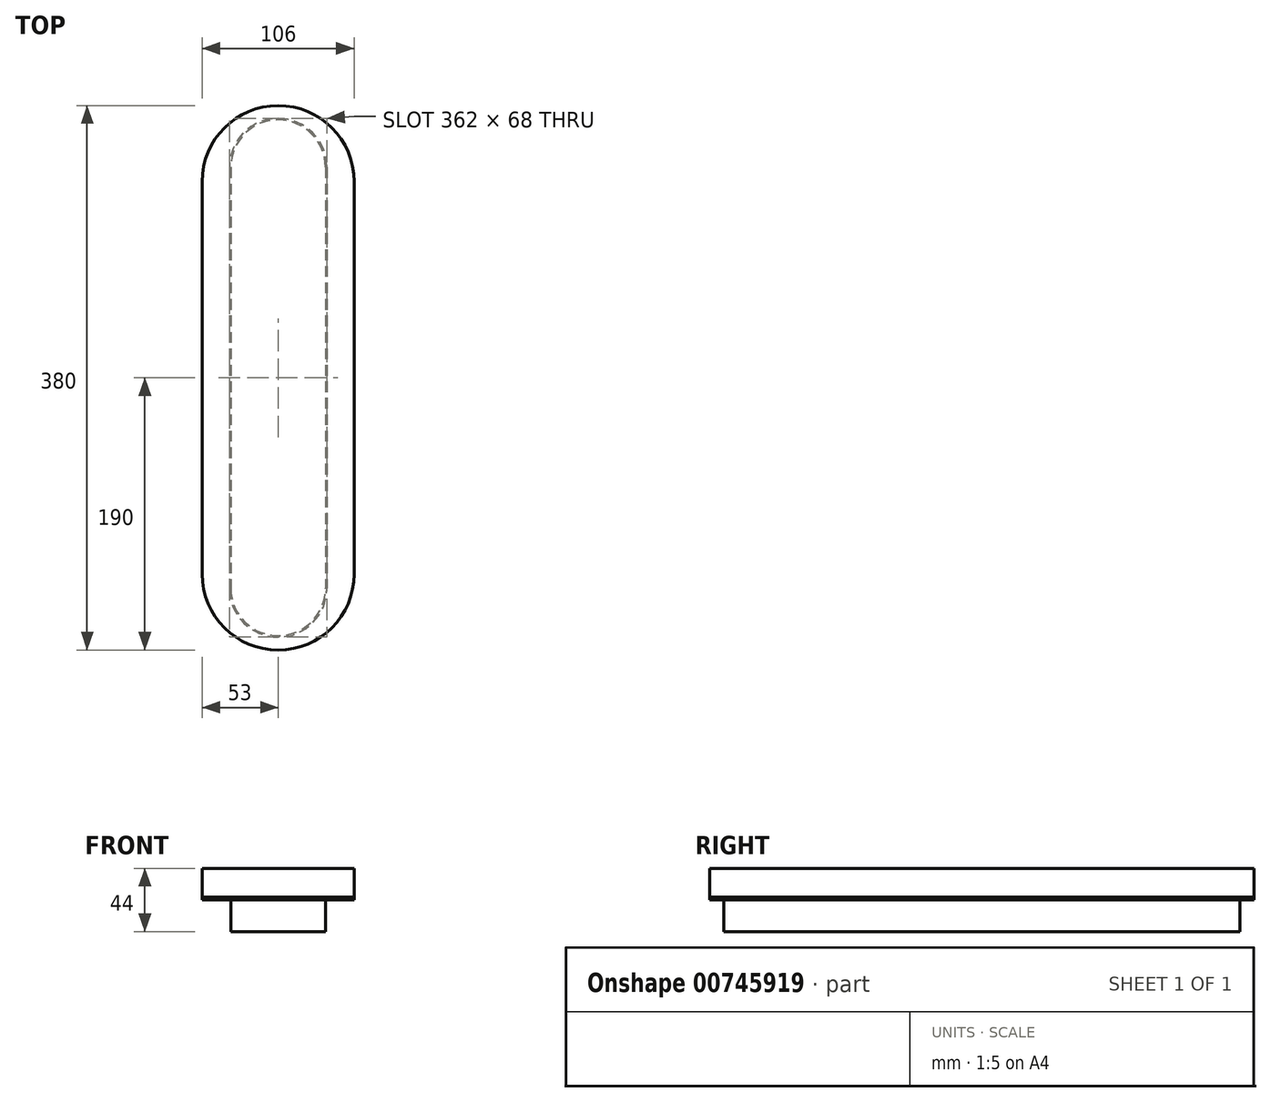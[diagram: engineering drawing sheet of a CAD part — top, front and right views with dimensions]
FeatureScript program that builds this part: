
annotation { "Feature Type Name" : "Feature", "Feature Type Description" : "" }
export const myFeature = defineFeature(function(context is Context, id is Id, definition is map)
    precondition{}
    {
        {
            var Q0;
            Q0=qCreatedBy(makeId("Top.planeOp"),FACE);
            var sketch = newSketch(context, id + "F0", { "sketchPlane" : qUnion([Q0])});
            skLineSegment(sketch, "E0.bottom", {"start": v(33, 147) * mm, "end": v(-33, 147) * mm});
            skLineSegment(sketch, "E0.top", {"start": v(33, -147) * mm, "end": v(-33, -147) * mm});
            skLineSegment(sketch, "E0.left", {"start": v(33, 147) * mm, "end": v(33, -147) * mm});
            skLineSegment(sketch, "E0.right", {"start": v(-33, 147) * mm, "end": v(-33, -147) * mm});
            skPoint(sketch, "E0.middle", {"position": v(0, 0) * mm});
            skArc(sketch, "E1", {"start": v(33, 147) * mm, "mid": v(0, 180) * mm, "end": v(-33, 147) * mm});
            skArc(sketch, "E2", {"start": v(-33, -147) * mm, "mid": v(0, -180) * mm, "end": v(33, -147) * mm});
            skLineSegment(sketch, "E3.bottom", {"start": v(53, -137) * mm, "end": v(-53, -137) * mm});
            skLineSegment(sketch, "E3.top", {"start": v(53, 137) * mm, "end": v(-53, 137) * mm});
            skLineSegment(sketch, "E3.left", {"start": v(53, -137) * mm, "end": v(53, 137) * mm});
            skLineSegment(sketch, "E3.right", {"start": v(-53, -137) * mm, "end": v(-53, 137) * mm});
            skArc(sketch, "E4", {"start": v(53, 137) * mm, "mid": v(0, 190) * mm, "end": v(-53, 137) * mm});
            skArc(sketch, "E5", {"start": v(-53, -137) * mm, "mid": v(0, -190) * mm, "end": v(53, -137) * mm});
            skLineSegment(sketch, "E6", {"start": v(-143.13, 190) * mm, "end": v(145.96, 190) * mm, "construction": true});
            skLineSegment(sketch, "E7", {"start": v(-154.64, -190) * mm, "end": v(161.47, -190) * mm, "construction": true});
            skLineSegment(sketch, "E8", {"start": v(0, 180) * mm, "end": v(180.44, 180) * mm, "construction": true});
            skLineSegment(sketch, "E9", {"start": v(0, -180) * mm, "end": v(180.44, -180) * mm, "construction": true});
            skSolve(sketch);
        }
        {
            var Q0;
            {var subQ0=sQuery(id+"F0.wireOp",EDGE,"E3.top");var subQ1=sQuery(id+"F0.wireOp",EDGE,"E0.left");var subQ2=makeQuery(id+"F0.imprint","INTERSECT",VERTEX,{"derivedFrom":[subQ1,subQ0]});Q0=makeQuery(id+"F0.imprint","IMPRINT",FACE,{"disambiguationData":[TD([[makeQuery(id+"F0.imprint","IMPRINT",EDGE,{"disambiguationData":[TD([[subQ2,-1.0]])],"derivedFrom":subQ1}),-1.0]])]});}
            var Q1;
            {var subQ0=sQuery(id+"F0.wireOp",EDGE,"E0.bottom");Q1=makeQuery(id+"F0.imprint","IMPRINT",FACE,{"disambiguationData":[TD([[makeQuery(id+"F0.imprint","IMPRINT",EDGE,{"derivedFrom":subQ0}),1.0]])]});}
            var Q2;
            Q2=makeQuery(id+"F0.imprint","IMPRINT",FACE,{"disambiguationData":[TD([[makeQuery(id+"F0.imprint","IMPRINT",EDGE,{"derivedFrom":sQuery(id+"F0.wireOp",EDGE,"E0.bottom")}),-1.0]])]});
            var Q3;
            {var subQ0=sQuery(id+"F0.wireOp",EDGE,"E0.top");Q3=makeQuery(id+"F0.imprint","IMPRINT",FACE,{"disambiguationData":[TD([[makeQuery(id+"F0.imprint","IMPRINT",EDGE,{"derivedFrom":subQ0}),-1.0]])]});}
            var Q4;
            Q4=makeQuery(id+"F0.imprint","IMPRINT",FACE,{"disambiguationData":[TD([[makeQuery(id+"F0.imprint","IMPRINT",EDGE,{"derivedFrom":sQuery(id+"F0.wireOp",EDGE,"E0.top")}),1.0]])]});
            extrude(context, id + "F1", {"entities" : qUnion([Q0, Q1, Q2, Q3, Q4]), "oppositeDirection" : true, "depth" : 44 * mm, "offsetDistance" : 25 * mm});
        }
        {
            var Q0;
            {var subQ5=sQuery(id+"F0.wireOp",EDGE,"E3.right");Q0=makeQuery(id+"F0.imprint","IMPRINT",FACE,{"disambiguationData":[TD([[makeQuery(id+"F0.imprint","IMPRINT",EDGE,{"derivedFrom":subQ5}),-1.0]])]});}
            var Q1;
            {var subQ4=sQuery(id+"F0.wireOp",EDGE,"E1");Q1=makeQuery(id+"F0.imprint","IMPRINT",FACE,{"disambiguationData":[TD([[makeQuery(id+"F0.imprint","IMPRINT",EDGE,{"derivedFrom":subQ4}),-1.0]])]});}
            var Q2;
            {var subQ5=sQuery(id+"F0.wireOp",EDGE,"E3.left");Q2=makeQuery(id+"F0.imprint","IMPRINT",FACE,{"disambiguationData":[TD([[makeQuery(id+"F0.imprint","IMPRINT",EDGE,{"derivedFrom":subQ5}),1.0]])]});}
            var Q3;
            {var subQ4=sQuery(id+"F0.wireOp",EDGE,"E2");Q3=makeQuery(id+"F0.imprint","IMPRINT",FACE,{"disambiguationData":[TD([[makeQuery(id+"F0.imprint","IMPRINT",EDGE,{"derivedFrom":subQ4}),-1.0]])]});}
            extrude(context, id + "F2", {"entities" : qUnion([Q0, Q1, Q2, Q3]), "operationType" : NewBodyOperationType.ADD, "oppositeDirection" : true, "depth" : 20 * mm, "offsetDistance" : 25 * mm});
        }
        {
            var Q0;
            Q0=makeQuery(id+"F2.opExtrude","CAP_FACE",FACE,{"disambiguationData":[OSD([sQuery(id+"F0.wireOp",EDGE,"E0.left"),sQuery(id+"F0.wireOp",EDGE,"E0.right"),sQuery(id+"F0.wireOp",EDGE,"E1"),sQuery(id+"F0.wireOp",EDGE,"E2"),sQuery(id+"F0.wireOp",EDGE,"E3.left"),sQuery(id+"F0.wireOp",EDGE,"E3.right"),sQuery(id+"F0.wireOp",EDGE,"E4"),sQuery(id+"F0.wireOp",EDGE,"E5")])],"isStart":false});
            var sketch = newSketch(context, id + "F3", { "sketchPlane" : qUnion([Q0])});
            skLineSegment(sketch, "E10.0", {"start": v(-53, 137) * mm, "end": v(-53, -137) * mm});
            skArc(sketch, "E10.1", {"start": v(-53, 137) * mm, "mid": v(0, 190) * mm, "end": v(53, 137) * mm});
            skLineSegment(sketch, "E10.2", {"start": v(53, 137) * mm, "end": v(53, -137) * mm});
            skArc(sketch, "E10.3", {"start": v(53, -137) * mm, "mid": v(0, -190) * mm, "end": v(-53, -137) * mm});
            skLineSegment(sketch, "E11.0", {"start": v(-34, -147) * mm, "end": v(-34, 147) * mm});
            skArc(sketch, "E11.1", {"start": v(34, -147) * mm, "mid": v(0, -181) * mm, "end": v(-34, -147) * mm});
            skLineSegment(sketch, "E11.2", {"start": v(34, -147) * mm, "end": v(34, 147) * mm});
            skArc(sketch, "E11.3", {"start": v(-34, 147) * mm, "mid": v(0, 181) * mm, "end": v(34, 147) * mm});
            skSolve(sketch);
        }
        {
            var Q0;
            Q0 = qSketchRegion(id + "F3", true);
            extrude(context, id + "F4", {"entities" : qUnion([Q0]), "depth" : 2 * mm, "offsetDistance" : 25 * mm});
        }
    });
